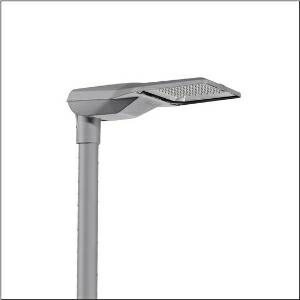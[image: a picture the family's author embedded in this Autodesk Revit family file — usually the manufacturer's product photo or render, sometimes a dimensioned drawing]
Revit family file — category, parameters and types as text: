
# Revit family: streetlight_sl_21_iq_midi___pl52_5xe3h41d08mb_c975
name_source: partatom
category: Lighting Fixtures
units: mm (PartAtom-declared; Revit-internal decimal feet)

## family parameters
Cut with Voids When Loaded = No
Host = Face
Light Source = No
Part Type = Normal
Room Calculation Point = No
Round Connector Dimension = Use Diameter
Shared = No

## types (1)
- --- (1 x LED, 20000 lm, 146.7 W, 4000K)
    Apparent Load = 147 VA
    CIE Flux Codes = 27 59 98 100 100
    Color Rendering = 70
    Color Temperature = 4000K
    Default Elevation = 1800 mm
    Description = Streetlight SL 21 iQ midi, mast luminaire, primary light control with lens, of PMMA, primary optical cover: cover, of toughened safety glass, transparent, light distribution: PL52, light emission: direct distribution, primary light characteristic: asymmetric, installation type: post-top, side-entry, LED, High Power LED, rated luminous flux: 20.000lm, luminous efficacy: 136lm/W, light colour: 740, colour temperature: 4000K, control gear: iQ-Comfort, control: Auto-Match, Temp-Guard, Lumen-Switch, Night-Set, Smart-Wire, Light-Fading, Desk-Remote (wireless, voltage-free reading and setting of iQ features in the workshop via application-optimized NFC function/RFID function), optimised constant luminous flux control (CLO 2.0), pre-setting: linear dimming characteristic, mains connection: 230..240V, AC, 50/60Hz, start of lifetime: 147W, end of service life: 161W, reduction: 62W, luminaire housing, of diecast aluminium, powder-coated, SITECO metallic grey (DB 702S), corrosivity category C5 high according to DIN EN ISO 12944, please order mast flange separately, inclination adjustable: 0°, 5°, 10°, 15°, sealing non-destructively replaceable, multi-level sealing system, length: 644mm, width: 335mm, height: 110mm, mast flange for spigot size: 42mm (side-entry): 5XC10008XM4, 60/48mm (side-entry/post-top): 5XC10108XM2, 76/60mm (side-entry/post-top): 5XC10108XM1, mounting height: 4..8m, protection rating (complete): IP66, insulation class (complete): insulation class II (safety insulation), certification: CE, ENEC, ENEC+, VDE, impact resistance: IK10, permissible operating ambient temperature for outdoor applications: -40..+50°C, standard-compliant lighting for roads and squares, packaging unit: 1 piece

Light Distribution: PL52
    Height = 111 mm
    Lamp = 1 x LED
    Lamp Light Flux = 20000 lm
    Lamp Power = 146.7 W
    Lamp count = 1
    Length = 644 mm
    Luminous efficacy = 136 lm/W
    Manufacturer = Siteco
    ModVariant = No
    Model = 5XE3H41D08MB
    Number of Poles = 1
    OnlyDefault = Yes
    Power Factor = 1
    Product Name = Streetlight SL 21 iQ midi | PL52
    Product group = mast luminaire | pylon top
    ProductGroupID = 6100
    Protection Class = Protection class II
    Protection Degree = IP 66
    RLX_Detail_Level = 1
    RLX_Emergency_Light_Flux = 0 lm
    RLX_Emergency_Type = 0
    RLX_Emergency_Type_DB = No
    RlxData = <blob elided: 36497 chars, md5=4f672835>
    Socket = socket
    Standby Power = 0 W
    System Light Flux = 20000 lm
    System Power = 147 W
    Type Comments = factory setting: luminous flux: 100 % | dim-lin: 254 | 753 mA
    Type Image = l_1004298.jpg
    URL = http://relux.com
    VarID = @adj_188205
    Voltage = 0 V
    Weight = 0.00 kg
    Width = 336 mm

## geometry (parser evidence)
native form markers: Blend x4, Sweep x8
no freeform markers — native parametric forms only
